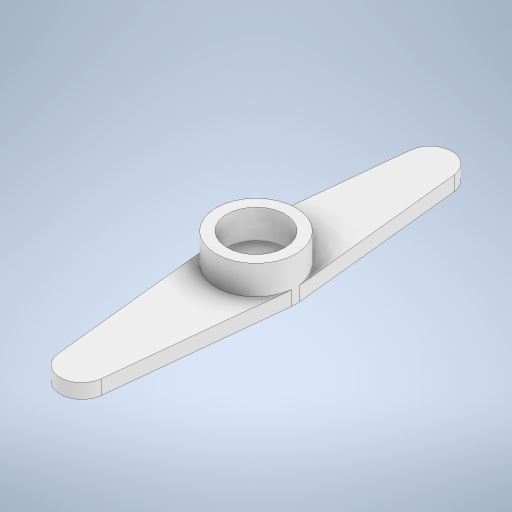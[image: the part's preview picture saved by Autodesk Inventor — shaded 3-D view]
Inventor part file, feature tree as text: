
AUTODESK INVENTOR PART (.ipt)
format: ipt  version: 2024 (Build 280153000, 153)  size: 259,072 bytes
history: native  units: in
note: dims shown in document units (in); Inventor stores cm internally (conversion verified against a paired STEP export)
features: extrude x2, sketch x2
ambient origin geometry x8: Origin, YZ Plane, XZ Plane, XY Plane, X Axis, Y Axis, Z Axis, Center Point
bodies: Solid1 (feature_tree)
feature tree (4):
  extrude  "Extrusion1"  Depth=0.1181in
  extrude  "Extrusion2"  Depth=0.0394in TaperAngle=0.0deg
  sketch  "Sketch1"  dims[d0=0.2165in d1=0.1181in]
  sketch  "Sketch2"  dims[d2=1.063in d3=0.0394in d4=0.0in d5=0.2165in d6=0.1575in d7=0.0787in d8=0.0in d9=0.0344in]
